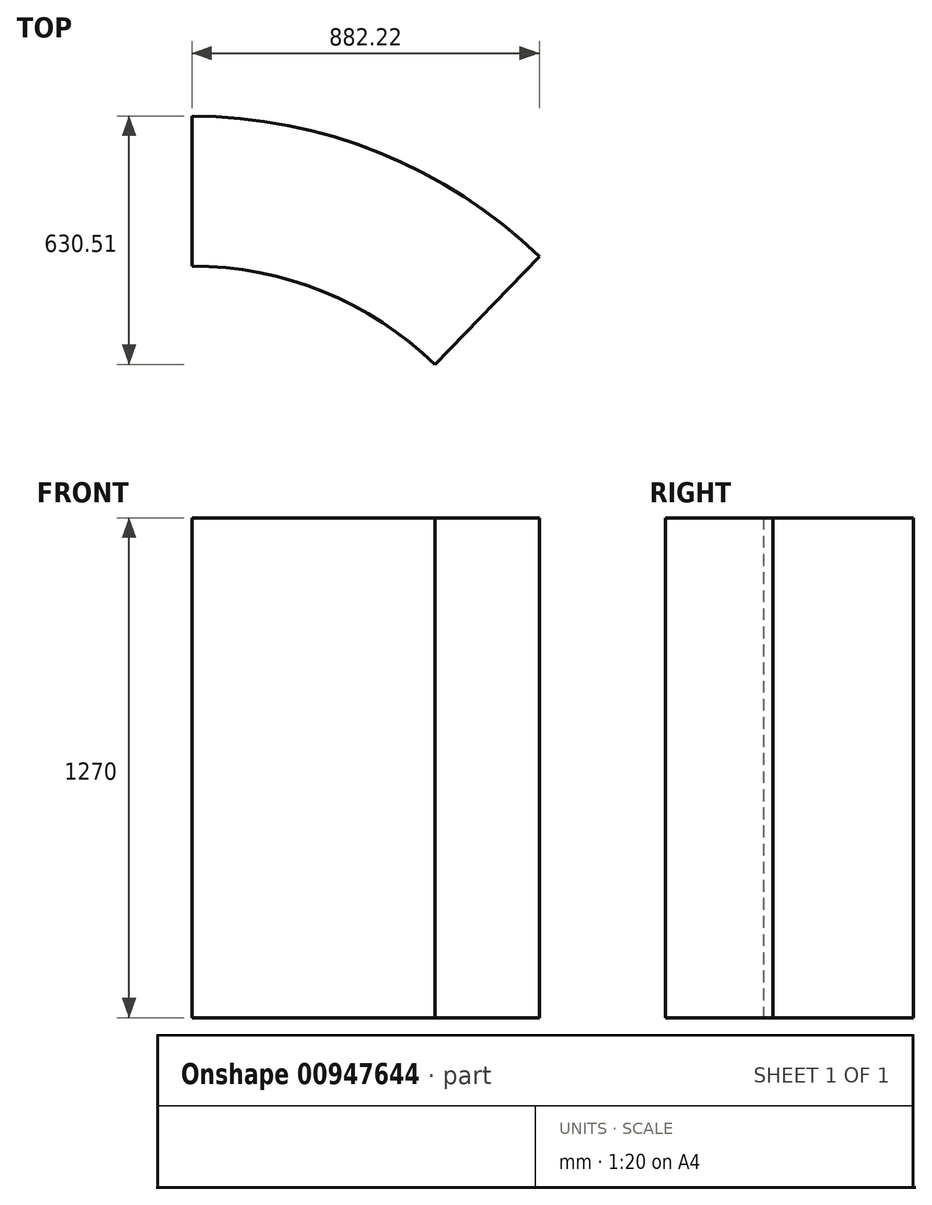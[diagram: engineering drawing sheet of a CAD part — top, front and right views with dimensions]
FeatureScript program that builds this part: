
annotation { "Feature Type Name" : "Feature", "Feature Type Description" : "" }
export const myFeature = defineFeature(function(context is Context, id is Id, definition is map)
    precondition{}
    {
        {
            var Q0;
            Q0=qCreatedBy(makeId("Top.planeOp"),FACE);
            var sketch = newSketch(context, id + "F0", { "sketchPlane" : qUnion([Q0])});
            skCircle(sketch, "E0", {"center": v(0, 0) * mm, "radius": 1270 * mm});
            skCircle(sketch, "E1", {"center": v(0, 0) * mm, "radius": 889 * mm});
            skSolve(sketch);
        }
        {
            var Q0;
            Q0=qCreatedBy(makeId("Top.planeOp"),FACE);
            var Q1;
            Q1=qCreatedBy(makeId("Top.planeOp"),FACE);
            var sketch = newSketch(context, id + "F1", { "sketchPlane" : qUnion([Q0, Q1])});
            skArc(sketch, "E2.0.0", {"start": v(617.55, 639.5) * mm, "mid": v(333.03, 824.27) * mm, "end": v(0, 889) * mm});
            skLineSegment(sketch, "E3", {"start": v(0, 889) * mm, "end": v(0, 1270) * mm});
            skLineSegment(sketch, "E4", {"start": v(882.22, 913.56) * mm, "end": v(617.55, 639.5) * mm});
            skArc(sketch, "E5", {"start": v(882.22, 913.56) * mm, "mid": v(475.75, 1177.52) * mm, "end": v(0, 1270) * mm});
            skSolve(sketch);
        }
        {
            var Q0;
            Q0 = qSketchRegion(id + "F1", true);
            extrude(context, id + "F2", {"entities" : qUnion([Q0]), "depth" : 1270 * mm, "offsetDistance" : 25.4 * mm});
        }
    });
